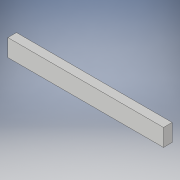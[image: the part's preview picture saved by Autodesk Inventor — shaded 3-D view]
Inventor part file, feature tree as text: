
AUTODESK INVENTOR PART (.ipt)
format: ipt  version: 2017 (Build 210142000, 142)  size: 89,600 bytes
history: native  units: in
note: dims shown in document units (in); Inventor stores cm internally (conversion verified against a paired STEP export)
features: extrude x1, sketch x1
ambient origin geometry x8: Origin, YZ Plane, XZ Plane, XY Plane, X Axis, Y Axis, Z Axis, Center Point
bodies: Solid1 (feature_tree)
feature tree (2):
  extrude  "Extrusion1"  Depth=2.0in
  sketch  "Sketch1"  dims[d0=18.0in d1=2.0in d2=1.0in d3=0.0in]
